# Revit family: MLR3-M1
name_source: partatom
category: Lighting Fixtures
units: mm (PartAtom-declared; Revit-internal decimal feet)

## family parameters
Cut with Voids When Loaded = No
Host = Face
Light Source = Yes
OmniClass Number = 23.80.70.11
OmniClass Title = Luminaries for Internal Lighting
Part Type = Normal
Room Calculation Point = No
Round Connector Dimension = Use Diameter
Shared = No

## types (1)
- MLR3-M1
    Apparent Load = 0 VA
    Cable Suspension = 0' - 0"
    Color Filter = 16777215
    Dimming Lamp Color Temperature Shift = <None>
    Emit Shape Visible in Rendering = No
    Emit from Rectangle Length = 4' - 0"
    Emit from Rectangle Width = 2' - 0"
    Fixture width = 0' - 3"
    Housing = Metal, Paint Finish, White, Matte
    Lamp = LED
    Lens = Acrylic
    Load Classifcation = Lighting
    Manufacturer = Mercury Lighting
    Model = MLR3-M1
    No of Hanging Points = 2
    Photometric Web File = mer12182822.28-MLR3-M-48-770-35K-ASO-A401-U.ies
    Tilt Angle = 90.00°
    URL = https://mercltg.com
    Voltage Comment = 120/277 UNV Volt

## geometry (parser evidence)
native form markers: Extrusion x1, Sweep x2
no freeform markers — native parametric forms only
